# Revit family: Toilet-Wall_Mount-KOHLER-Kingston-K-4323_1
name_source: partatom
category: Plumbing Fixtures
units: mm (PartAtom-declared; Revit-internal decimal feet)

## family parameters
Cut with Voids When Loaded = No
Host = Face
OmniClass Number = 23.31.19.00
OmniClass Title = Toilets
Part Type = Normal
Room Calculation Point = No
Round Connector Dimension = Use Diameter
Shared = No

## types (2) — shared parameters
ADA Compliant = Yes
Assembly Code = D2010100
CW Connection = Yes
Cold Water Inlet = Cold Water Inlet
Date Modified = 05/18/2023
Default Elevation = 0"
Finish = Kohler-Vitreous_China-0-White
Flow Rate = 0 GPM
Flush Rate- GPF = 1.6 GPF
Flush Rate- LPF = 6.0 LPF
HW Connection = No
Height = 16 5/8"
Hot Water Inlet = Hot Water Inlet
Length = 26 1/2"
Manufacturer = Kohler Co.
Master Format 2014 = 22 42 13.13
Master Format 2014 Name = Residential Water Closets
Material = Viterous China
Pressure = 0.00 psi
Product Documentation Link = https://www.us.kohler.com
Product Name = Kingston
Product Page URL = http://www.us.kohler.com
Rough-In = 5"
Seat Included = No
URL = https://www.us.kohler.com
Vent Connection = No
Waste Connection = Yes
Waste Water Outlet = Waste Water Outlet
WaterSense Certified = No
Width = 16 3/4"

## per-type parameters (varying)
| type | 4323 | 4323-L | Description | Model | Type |
| With Lugs, 0-White | No | Yes | Wall-mount rear spud flushometer bowl with bedpan lugs | K-4323-L-0 | 1 |
| 0-White | Yes | No | Wall-mount rear spud flushometer bowl | K-4323-0 | 2 |

## geometry (parser evidence)
native form markers: Sweep x5
no freeform markers — native parametric forms only
